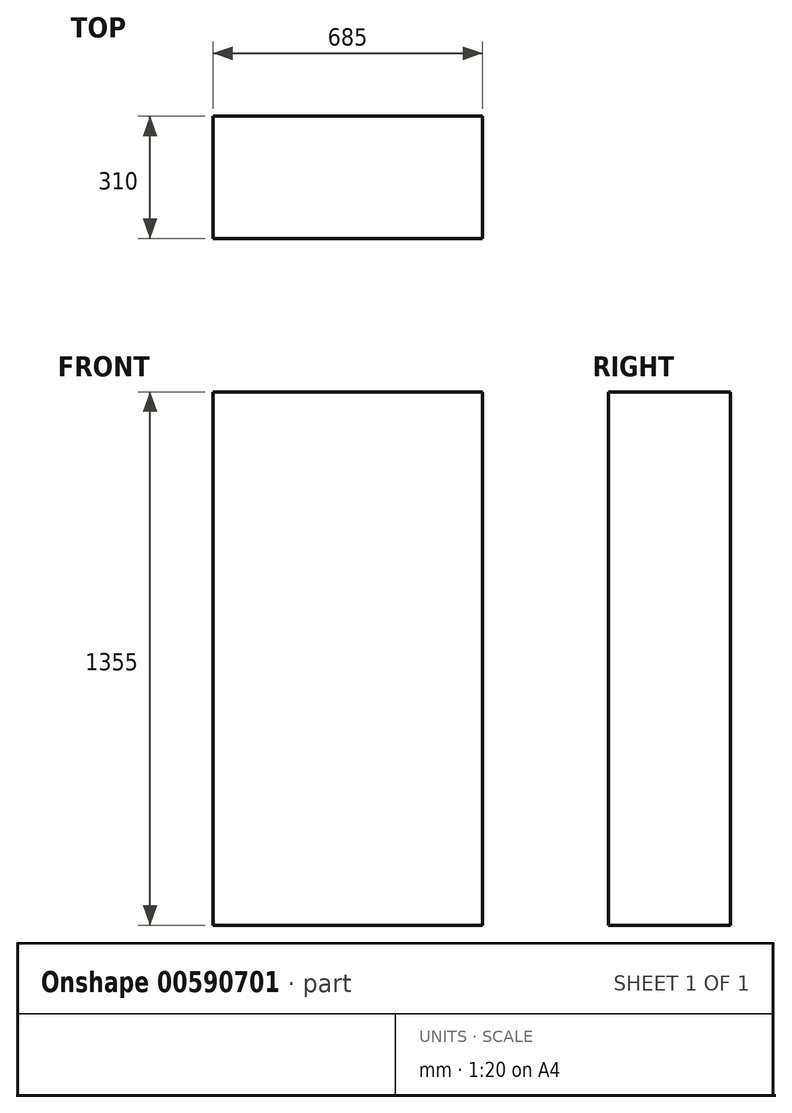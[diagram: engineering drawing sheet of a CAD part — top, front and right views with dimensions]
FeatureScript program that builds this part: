
annotation { "Feature Type Name" : "Feature", "Feature Type Description" : "" }
export const myFeature = defineFeature(function(context is Context, id is Id, definition is map)
    precondition{}
    {
        {
            var Q0;
            Q0=qCreatedBy(makeId("Front.planeOp"),FACE);
            var sketch = newSketch(context, id + "F0", { "sketchPlane" : qUnion([Q0])});
            skLineSegment(sketch, "E0.bottom", {"start": v(-342.5, 677.5) * mm, "end": v(342.5, 677.5) * mm});
            skLineSegment(sketch, "E0.top", {"start": v(-342.5, -677.5) * mm, "end": v(342.5, -677.5) * mm});
            skLineSegment(sketch, "E0.left", {"start": v(-342.5, 677.5) * mm, "end": v(-342.5, -677.5) * mm});
            skLineSegment(sketch, "E0.right", {"start": v(342.5, 677.5) * mm, "end": v(342.5, -677.5) * mm});
            skPoint(sketch, "E0.middle", {"position": v(0, 0) * mm});
            skSolve(sketch);
        }
        {
            var Q0;
            Q0=makeQuery(id+"F0.imprint","IMPRINT",FACE,{"disambiguationData":[TD([[makeQuery(id+"F0.imprint","IMPRINT",EDGE,{"derivedFrom":sQuery(id+"F0.wireOp",EDGE,"E0.bottom")}),-1.0]])]});
            extrude(context, id + "F1", {"entities" : qUnion([Q0]), "endBound" : BoundingType.SYMMETRIC, "depth" : 310 * mm, "offsetDistance" : 25 * mm});
        }
    });
